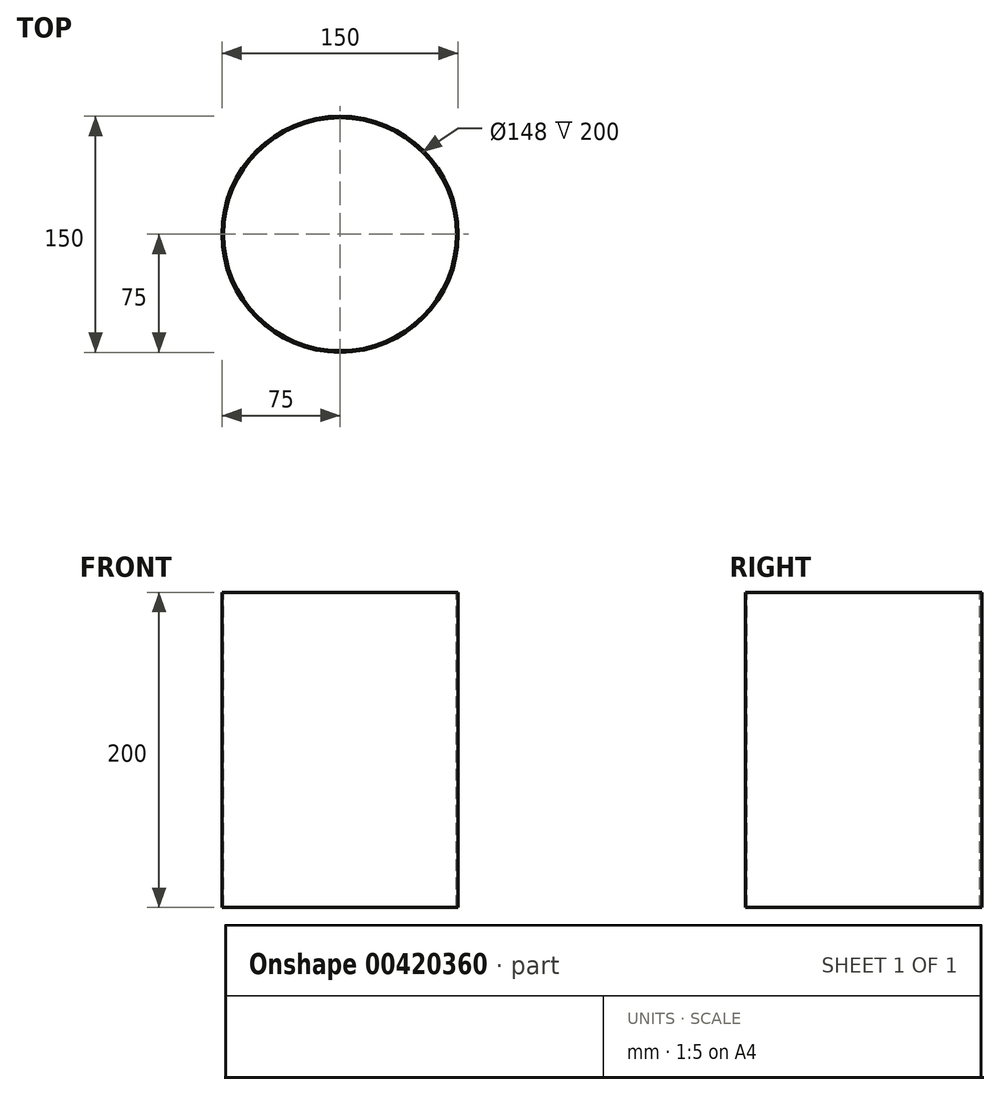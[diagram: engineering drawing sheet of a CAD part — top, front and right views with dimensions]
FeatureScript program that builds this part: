
annotation { "Feature Type Name" : "Feature", "Feature Type Description" : "" }
export const myFeature = defineFeature(function(context is Context, id is Id, definition is map)
    precondition{}
    {
        {
            var Q0;
            Q0=qCreatedBy(makeId("Top.planeOp"),FACE);
            var sketch = newSketch(context, id + "F0", { "sketchPlane" : qUnion([Q0])});
            skCircle(sketch, "E0", {"center": v(0, 0) * mm, "radius": 75 * mm});
            skSolve(sketch);
        }
        {
            var Q0;
            Q0=makeQuery(id+"F0.imprint","IMPRINT",FACE,{"disambiguationData":[TD([[makeQuery(id+"F0.imprint","IMPRINT",EDGE,{"derivedFrom":sQuery(id+"F0.wireOp",EDGE,"E0")}),1.0]])]});
            var sketch = newSketch(context, id + "F1", { "sketchPlane" : qUnion([Q0])});
            skLineSegment(sketch, "E1", {"start": v(-14.64, 75.04) * mm, "end": v(15.36, 75.04) * mm});
            skLineSegment(sketch, "E2", {"start": v(-14.64, 75.04) * mm, "end": v(-14.64, 72.33) * mm});
            skLineSegment(sketch, "E3", {"start": v(-14.64, 72.33) * mm, "end": v(15.39, 72.33) * mm});
            skLineSegment(sketch, "E4", {"start": v(15.39, 72.33) * mm, "end": v(15.36, 75.04) * mm});
            skSolve(sketch);
        }
        {
            var Q0;
            Q0=makeQuery(id+"F0.imprint","IMPRINT",FACE,{"disambiguationData":[TD([[makeQuery(id+"F0.imprint","IMPRINT",EDGE,{"derivedFrom":sQuery(id+"F0.wireOp",EDGE,"E0")}),1.0]])]});
            extrude(context, id + "F2", {"entities" : qUnion([Q0]), "depth" : 200 * mm});
        }
        {
            var Q0;
            Q0=makeQuery(id+"F2.opExtrude","CAP_FACE",FACE,{"disambiguationData":[OSD([sQuery(id+"F0.wireOp",EDGE,"E0")])],"isStart":false});
            var sketch = newSketch(context, id + "F3", { "sketchPlane" : qUnion([Q0])});
            skCircle(sketch, "E5", {"center": v(0, 0) * mm, "radius": 74 * mm});
            skSolve(sketch);
        }
        {
            var Q0;
            Q0 = qSketchRegion(id + "F3", true);
            extrude(context, id + "F4", {"entities" : qUnion([Q0]), "operationType" : NewBodyOperationType.REMOVE, "oppositeDirection" : true, "depth" : 200 * mm});
        }
        {
            var Q0;
            {var subQ0=sQuery(id+"F1.wireOp",EDGE,"E3");Q0=makeQuery(id+"F1.imprint","IMPRINT",FACE,{"disambiguationData":[TD([[makeQuery(id+"F1.imprint","IMPRINT",EDGE,{"derivedFrom":subQ0}),1.0]])]});}
            extrude(context, id + "F5", {"entities" : qUnion([Q0]), "operationType" : NewBodyOperationType.REMOVE, "oppositeDirection" : true, "depth" : 200 * mm});
        }
    });
